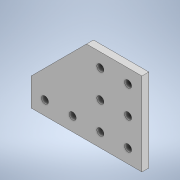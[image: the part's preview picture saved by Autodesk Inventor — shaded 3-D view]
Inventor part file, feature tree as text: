
AUTODESK INVENTOR PART (.ipt)
format: ipt  version: 2020 (Build 240168000, 168)  size: 117,760 bytes
history: native  units: in
note: dims shown in document units (in); Inventor stores cm internally (conversion verified against a paired STEP export)
features: extrude x1, sketch x1
ambient origin geometry x8: Origin, YZ Plane, XZ Plane, XY Plane, X Axis, Y Axis, Z Axis, Center Point
bodies: Solid1 (feature_tree)
feature tree (2):
  extrude  "Extrusion1"  Depth=3.0in
  sketch  "Sketch1"  dims[d0=4.0in d1=3.0in d2=1.0in d3=0.256in d4=0.5in d5=0.5in d6=1.5748in d8=1.0in d9=0.3937in d11=1.0in d13=1.1811in d15=1.0in d16=0.3937in d18=1.0in d20=2.0in d21=0.25in d22=0.0in]
